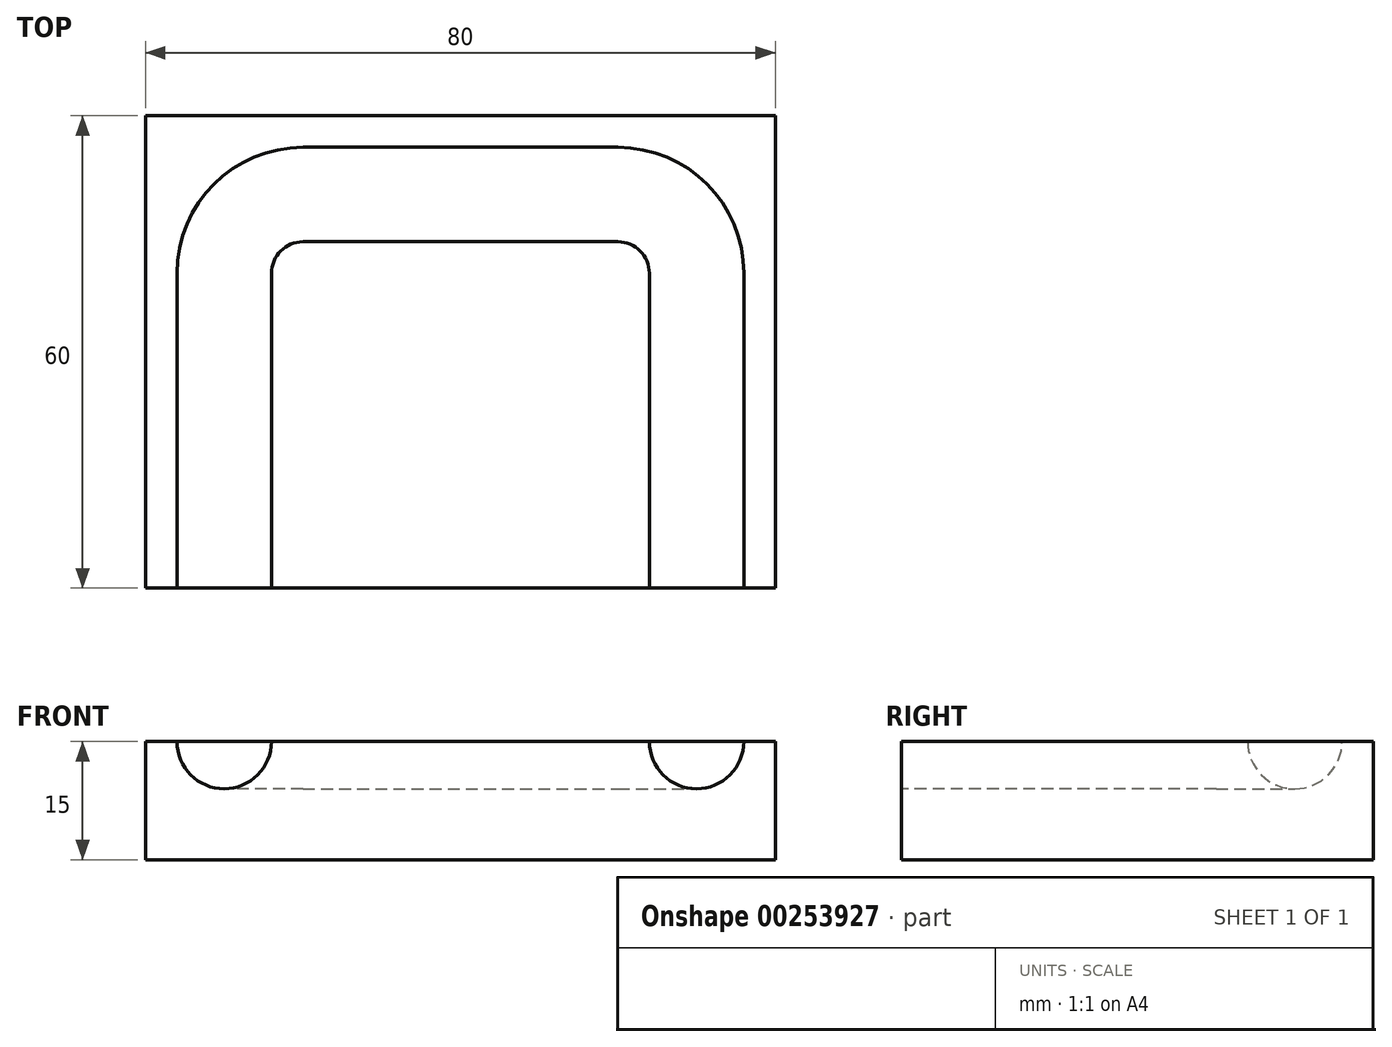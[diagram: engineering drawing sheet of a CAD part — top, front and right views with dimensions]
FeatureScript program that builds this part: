
annotation { "Feature Type Name" : "Feature", "Feature Type Description" : "" }
export const myFeature = defineFeature(function(context is Context, id is Id, definition is map)
    precondition{}
    {
        {
            var Q0;
            Q0=qCreatedBy(makeId("Top.planeOp"),FACE);
            var sketch = newSketch(context, id + "F0", { "sketchPlane" : qUnion([Q0])});
            skLineSegment(sketch, "E0.bottom", {"start": v(40, -30) * mm, "end": v(-40, -30) * mm});
            skLineSegment(sketch, "E0.top", {"start": v(40, 30) * mm, "end": v(-40, 30) * mm});
            skLineSegment(sketch, "E0.left", {"start": v(40, -30) * mm, "end": v(40, 30) * mm});
            skLineSegment(sketch, "E0.right", {"start": v(-40, -30) * mm, "end": v(-40, 30) * mm});
            skPoint(sketch, "E0.middle", {"position": v(0, 0) * mm});
            skSolve(sketch);
        }
        {
            var Q0;
            Q0=makeQuery(id+"F0.imprint","IMPRINT",FACE,{"disambiguationData":[TD([[makeQuery(id+"F0.imprint","IMPRINT",EDGE,{"derivedFrom":sQuery(id+"F0.wireOp",EDGE,"E0.bottom")}),-1.0]])]});
            extrude(context, id + "F1", {"entities" : qUnion([Q0]), "depth" : 15 * mm});
        }
        {
            var Q0;
            Q0=makeQuery(id+"F1.opExtrude","CAP_FACE",FACE,{"disambiguationData":[OSD([sQuery(id+"F0.wireOp",EDGE,"E0.bottom"),sQuery(id+"F0.wireOp",EDGE,"E0.top"),sQuery(id+"F0.wireOp",EDGE,"E0.left"),sQuery(id+"F0.wireOp",EDGE,"E0.right")])],"isStart":false});
            var sketch = newSketch(context, id + "F2", { "sketchPlane" : qUnion([Q0])});
            skLineSegment(sketch, "E1", {"start": v(-30, -30) * mm, "end": v(-30, 10) * mm});
            skLineSegment(sketch, "E2", {"start": v(-20, 20) * mm, "end": v(20, 20) * mm});
            skLineSegment(sketch, "E3", {"start": v(30, 10) * mm, "end": v(30, -30) * mm});
            skPoint(sketch, "E4.visualSharp", {"position": v(-30, 20) * mm});
            skArc(sketch, "E4.filletArc", {"start": v(-20, 20) * mm, "mid": v(-27.07, 17.07) * mm, "end": v(-30, 10) * mm});
            skPoint(sketch, "E5.visualSharp", {"position": v(30, 20) * mm});
            skArc(sketch, "E5.filletArc", {"start": v(30, 10) * mm, "mid": v(27.07, 17.07) * mm, "end": v(20, 20) * mm});
            skSolve(sketch);
        }
        {
            var Q0;
            Q0=makeQuery(id+"F1.opExtrude","SWEPT_FACE",FACE,{"disambiguationData":[OSD([sQuery(id+"F0.wireOp",EDGE,"E0.bottom")])]});
            var sketch = newSketch(context, id + "F3", { "sketchPlane" : qUnion([Q0])});
            skArc(sketch, "E6", {"start": v(-36, 15) * mm, "mid": v(-30, 9) * mm, "end": v(-24, 15) * mm});
            skLineSegment(sketch, "E7", {"start": v(-36, 15) * mm, "end": v(-24, 15) * mm});
            skSolve(sketch);
        }
        {
            var Q0;
            Q0=makeQuery(id+"F3.imprint","IMPRINT",FACE,{"disambiguationData":[TD([[makeQuery(id+"F3.imprint","IMPRINT",EDGE,{"derivedFrom":sQuery(id+"F3.wireOp",EDGE,"E6")}),1.0]])]});
            var Q1;
            Q1=sQuery(id+"F2.wireOp",EDGE,"E1");
            var Q2;
            Q2=sQuery(id+"F2.wireOp",EDGE,"E4.filletArc");
            var Q3;
            Q3=sQuery(id+"F2.wireOp",EDGE,"E2");
            var Q4;
            Q4=sQuery(id+"F2.wireOp",EDGE,"E5.filletArc");
            var Q5;
            Q5=sQuery(id+"F2.wireOp",EDGE,"E3");
            sweep(context, id + "F4", {"operationType" : NewBodyOperationType.REMOVE, "profiles" : qUnion([Q0]), "path" : qUnion([Q1, Q2, Q3, Q4, Q5])});
        }
    });
